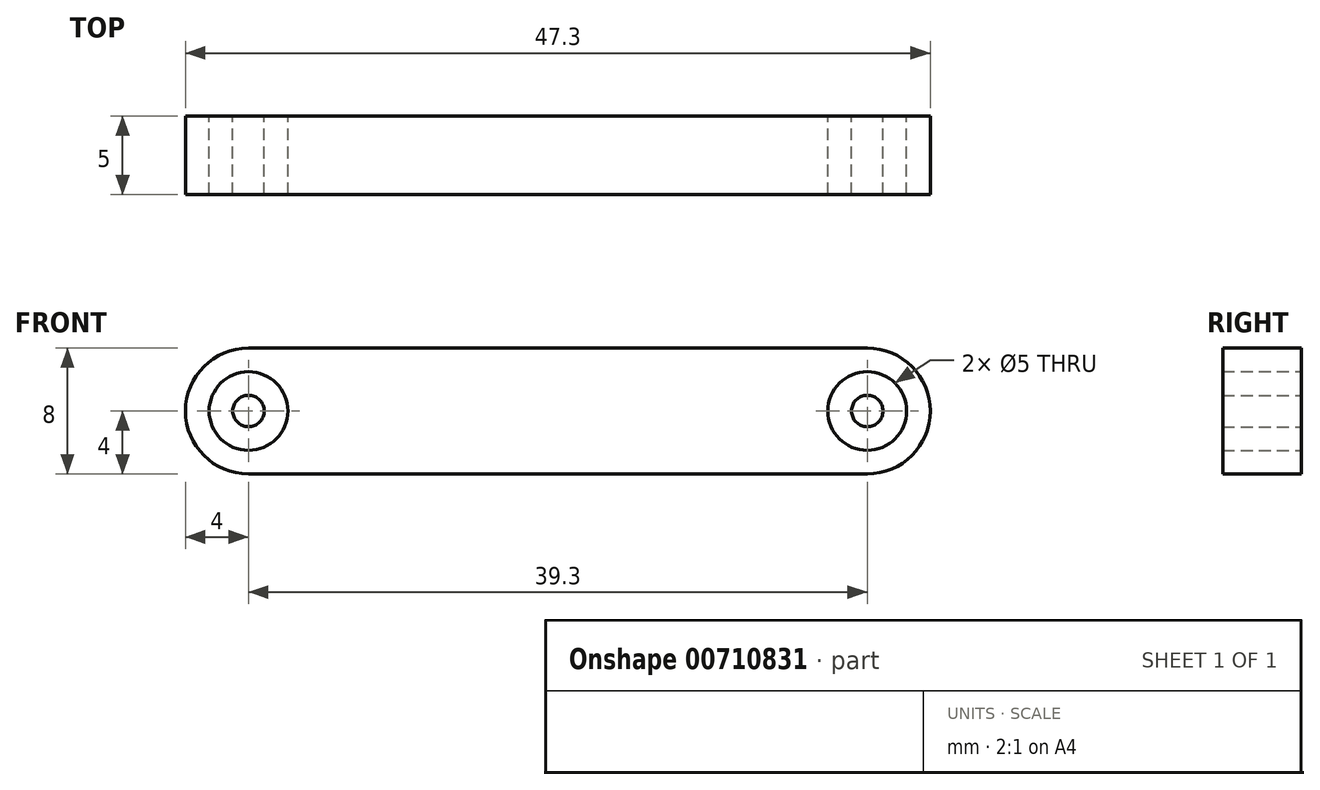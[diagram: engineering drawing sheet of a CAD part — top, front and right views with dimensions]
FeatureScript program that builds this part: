
annotation { "Feature Type Name" : "Feature", "Feature Type Description" : "" }
export const myFeature = defineFeature(function(context is Context, id is Id, definition is map)
    precondition{}
    {
        {
            var Q0;
            Q0=qCreatedBy(makeId("Front.planeOp"),FACE);
            var sketch = newSketch(context, id + "F0", { "sketchPlane" : qUnion([Q0])});
            skCircle(sketch, "E0", {"center": v(0, 0) * mm, "radius": 1 * mm});
            skCircle(sketch, "E1", {"center": v(0, 0) * mm, "radius": 2.5 * mm});
            skArc(sketch, "E2", {"start": v(0, 4) * mm, "mid": v(-4, 0) * mm, "end": v(0, -4) * mm});
            skCircle(sketch, "E3", {"center": v(39.3, 0) * mm, "radius": 1 * mm});
            skCircle(sketch, "E4", {"center": v(39.3, 0) * mm, "radius": 2.5 * mm});
            skArc(sketch, "E5", {"start": v(39.3, -4) * mm, "mid": v(43.3, 0) * mm, "end": v(39.3, 4) * mm});
            skLineSegment(sketch, "E6", {"start": v(0, 4) * mm, "end": v(39.3, 4) * mm});
            skLineSegment(sketch, "E7", {"start": v(0, -4) * mm, "end": v(39.3, -4) * mm});
            skSolve(sketch);
        }
        {
            var Q0;
            Q0=makeQuery(id+"F0.imprint","IMPRINT",FACE,{"disambiguationData":[TD([[makeQuery(id+"F0.imprint","IMPRINT",EDGE,{"derivedFrom":sQuery(id+"F0.wireOp",EDGE,"E1")}),-1.0]])]});
            var Q1;
            Q1=makeQuery(id+"F0.imprint","IMPRINT",FACE,{"disambiguationData":[TD([[makeQuery(id+"F0.imprint","IMPRINT",EDGE,{"derivedFrom":sQuery(id+"F0.wireOp",EDGE,"E0")}),1.0]])]});
            var Q2;
            Q2=makeQuery(id+"F0.imprint","IMPRINT",FACE,{"disambiguationData":[TD([[makeQuery(id+"F0.imprint","IMPRINT",EDGE,{"derivedFrom":sQuery(id+"F0.wireOp",EDGE,"E3")}),1.0]])]});
            extrude(context, id + "F1", {"entities" : qUnion([Q0, Q1, Q2]), "depth" : 5 * mm, "offsetDistance" : 25 * mm});
        }
    });
